# Revit family: Furniture_Table_STIKS 8.1
name_source: partatom
category: Furniture
units: mm (PartAtom-declared; Revit-internal decimal feet)

## family parameters
Always vertical = No
Cut with Voids When Loaded = No
OmniClass Number = 23.21.23.15.17
Room Calculation Point = No
Shared = No
Work Plane-Based = Yes

## types (3) — shared parameters
BIMobject category = Table
BIMobject category code = furniture-table
BIMobject main category = Furniture
BIMobject main category code = furniture
Brand url = https://www.sandlerseating.com
Description = Table
Design country = Brasil
Edition number = 1
Frame Material = Wood - Black Wanut
IFC Classification = Furnishing Element
Manufacturer = Sandler
Manufacturer country = USA
Manufacturer name = Sandler
Masterformat 2014 Code = 12 48 43.13
Masterformat 2014 Description = Table Mats
Model = STICKS 8.1
OmniClass Code = 23-21 23 15 17
Product Guid = ??
Product SKU = ??
Product data url = https://www.sandlerseating.com
Product family = Furniture
Product group = Table
Product name = STICKS 8.1
Product url = https://www.sandlerseating.com
QR code = https://www.sandlerseating.com
Top Material = Wood - Lacquered Wood - C49 Anthracite
Uniformat II Description = Movable Furnishings
zero-valued in all types: Default Elevation

## per-type parameters (varying)
| type | Raio Top |
| STICKS 8.1 - TOP 24" | 304.8 mm  [stored 1 ft] |
| STICKS 8.1 - TOP 28" | 355.6 mm  [stored 1.16667 ft] |
| STICKS 8.1 - TOP 32" | 406.4 mm  [stored 1.33333 ft] |

note: [stored X ft] marks values corroborated as IEEE doubles in the binary element streams (Revit-internal decimal feet)

## geometry (parser evidence)
native form markers: Blend x2, Sweep x3
no freeform markers — native parametric forms only
